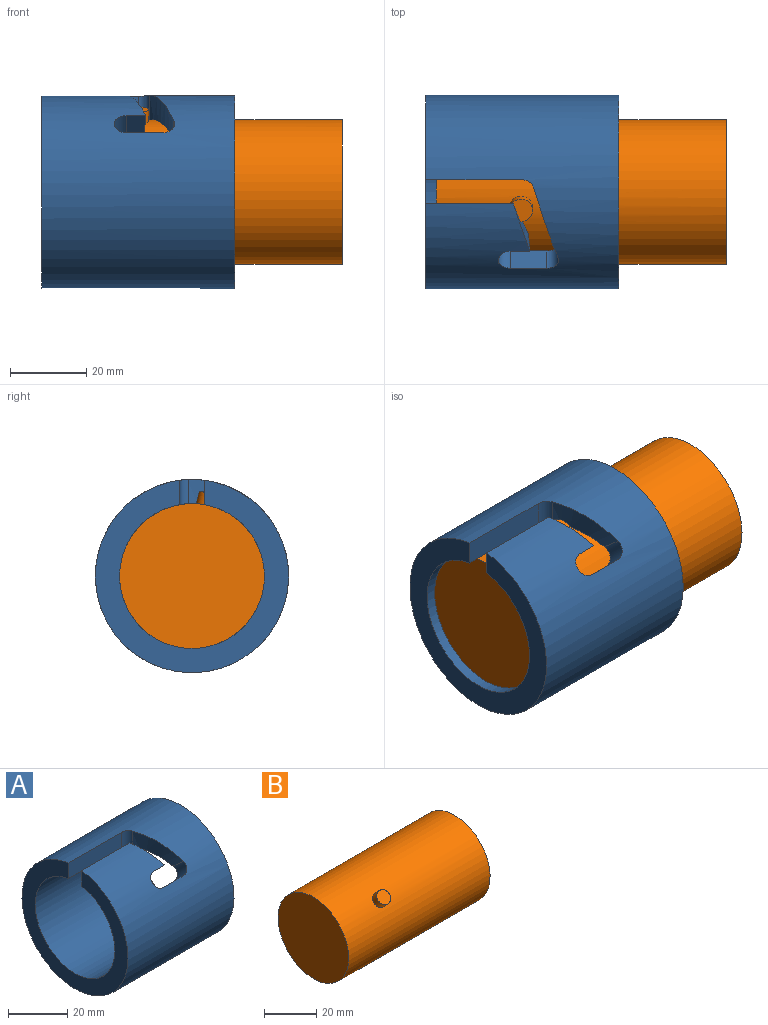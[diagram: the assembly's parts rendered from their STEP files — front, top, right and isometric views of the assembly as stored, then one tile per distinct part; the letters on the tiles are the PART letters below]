
ASSEMBLY  parts=2 mates=1
PART A: 13 faces, bbox 50.8x50.8x51.1 mm
  f0: cylinder r=19.05mm len=50.8mm, axis (-1,0,0), area 5745mm2, adj f2,f3,f4,f5,f6,f7,f8,f9
  f1: cylinder r=25.4mm len=50.8mm, axis (-1,0,0), area 7741.5mm2, adj f2,f3,f4,f5,f6,f7,f8,f9
  f2: plane 50.8x50.8mm, normal (1,0,0), area 886.7mm2, adj f0,f1
  f3: plane 50.8x50.6mm, normal (-1,0,0), area 846.3mm2, adj f0,f1,f5,f6
  f4: cylinder r=3.17mm len=6.6mm, axis (0,0,-1), area 25.6mm2, adj f0,f1,f5,f12
  f5: plane 25.4x6.42mm, normal (0,-1,0), area 163mm2, adj f0,f1,f3,f4
  f6: plane 23.31x6.42mm, normal (0,1,0), area 148.7mm2, adj f0,f1,f3,f11
  f7: cylinder r=3.17mm len=8.01mm, axis (0,0.71,-0.71), area 39.9mm2, adj f0,f1,f8,f12
  f8: plane 9.53x4.54mm, normal (0,0.71,0.71), area 61.1mm2, adj f0,f1,f7,f9
  f9: cylinder r=3.17mm len=9.17mm, axis (0,0.71,-0.71), area 63.7mm2, adj f0,f1,f8,f10
  f10: plane 5.17x4.54mm, normal (0,-0.71,-0.71), area 31.9mm2, adj f0,f1,f9,f11
  f11: bspline ~21.52x18.75mm, area 74.9mm2, adj f0,f1,f6,f10
  f12: bspline ~22.48x17.34mm, area 116.1mm2, adj f0,f1,f4,f7
PART B: 5 faces, bbox 76.2x38.1x38.1 mm
  f0: cylinder r=19.05mm len=76.2mm, axis (-1,0,0), area 9091.4mm2, adj f1,f2,f4
  f1: plane 38.1x38.1mm, normal (1,0,0), area 1140.1mm2, adj f0
  f2: plane 38.1x38.1mm, normal (-1,0,0), area 1140.1mm2, adj f0
  f3: plane 6.1x4.31mm, normal (0,-0.71,0.71), area 29.2mm2, adj f4
  f4: cylinder r=3.05mm len=6.73mm, axis (0,-0.71,0.71), area 63.2mm2, adj f0,f3
PLACE A at identity fixed
PLACE B rot(axis=(-1,0,0),32.3deg) t=(2.81,0,0)mm
MATE cylindrical B.f0 <-> A.f0  axis (-1,0,0) through (40.91,0,0)mm
